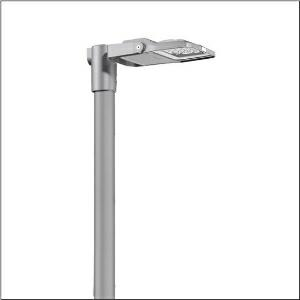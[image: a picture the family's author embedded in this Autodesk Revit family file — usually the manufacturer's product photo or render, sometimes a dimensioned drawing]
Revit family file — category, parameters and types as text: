
# Revit family: floodlight_fl_21_iq_micro___pl33t_5xa7761a2f3a_d57c
name_source: partatom
category: Lighting Fixtures
units: mm (PartAtom-declared; Revit-internal decimal feet)

## family parameters
Cut with Voids When Loaded = No
Host = Face
Light Source = No
Part Type = Normal
Room Calculation Point = No
Round Connector Dimension = Use Diameter
Shared = No

## types (1)
- --- (1 x LED, 2930 lm, 23.1 W, 3000K)
    Apparent Load = 23 VA
    CIE Flux Codes = 26 75 99 100 100
    Color Rendering = 70
    Color Temperature = 3000K
    Default Elevation = 1800 mm
    Description = Floodlight FL 21 iQ micro, floodlight, primary light control with lens, of PMMA, primary optical cover: protective disc, of toughened safety glass, transparent, light distribution: PL33T, light emission: direct distribution, installation type: surface-mounted, lamps: LED, High Power LED, rated values: 2.930lm | 23,1W | 126,8lm/W (begin service life); end service life: 2.930lm | 23,8W; at 50% lumin. flux: 1.465lm | 11W | 133,2lm/W, colour temperature: 3000K, colour rendering: CRI > 70, light colour: 730, light setting 1 begin service life: 100% | 2.930lm | 23,1W | 126,8lm/W | 3.000K, light setting 1 end service life: 23,8W, further light settings possible, control: optimised constant luminous flux control (CLO 2.0), Desk-Remote (wireless, voltage-free reading and setting of iQ features in the workshop via application-optimized NFC function/RFID function), Light-Fading, Smart-Wire, Night-Set, Lumen-Switch, Temp-Guard, Auto-Match, pre-setting: linear dimming characteristic, with terminal, 6-pole, mains connection: 220..240V, AC, 50/60Hz, luminaire housing, of diecast aluminium, powder-coated, SITECO metallic grey (DB 702S), corrosivity category C5 mid according to DIN EN ISO 12944suitable for swimming poolschlorine-resistant, sealing non-destructively replaceable, please order mast flange separately, mast bracket, of steel, galvanised, powder-coated, SITECO metallic grey (DB 702S), protection rating (complete): IP66, insulation class (complete): insulation class II (safety insulation), certification: CE, ENEC, VDE, protection symbol: D, impact resistance: IK07, permissible operating ambient temperature: -40..+40°C, permissible operating ambient temperature for outdoor applications: -40..+50°C, standard: DIN EN 12944, LABS conformity tested according to VDMA 24364:2018-05, packaging unit: 1 piece

Light Distribution: PL33T
    Height = 65 mm
    Lamp = 1 x LED
    Lamp Light Flux = 2930 lm
    Lamp Power = 23.1 W
    Lamp count = 1
    Length = 312 mm
    Luminous efficacy = 127 lm/W
    Manufacturer = Siteco
    ModVariant = No
    Model = 5XA7761A2F3A
    Number of Poles = 1
    OnlyDefault = Yes
    Power Factor = 1
    Product Name = Floodlight FL 21 iQ micro | PL33T
    Product group = floodlight | pylon top
    ProductGroupID = 6101
    Protection Class = Protection class II
    Protection Degree = IP 66
    RLX_Detail_Level = 1
    RLX_Emergency_Light_Flux = 0 lm
    RLX_Emergency_Type = 0
    RLX_Emergency_Type_DB = No
    RlxData = <blob elided: 102141 chars, md5=e5d6dce5>
    Socket = socket
    Standby Power = 0 W
    System Light Flux = 2930 lm
    System Power = 23 W
    Type Comments = factory setting: luminous flux: 100 % | dim-lin: 254 | 455 mA
    Type Image = l_1007121.jpg
    URL = http://relux.com
    VarID = @adj_147713
    Voltage = 0 V
    Weight = 0.00 kg
    Width = 230 mm

## geometry (parser evidence)
native form markers: Blend x4, Sweep x12
no freeform markers — native parametric forms only
